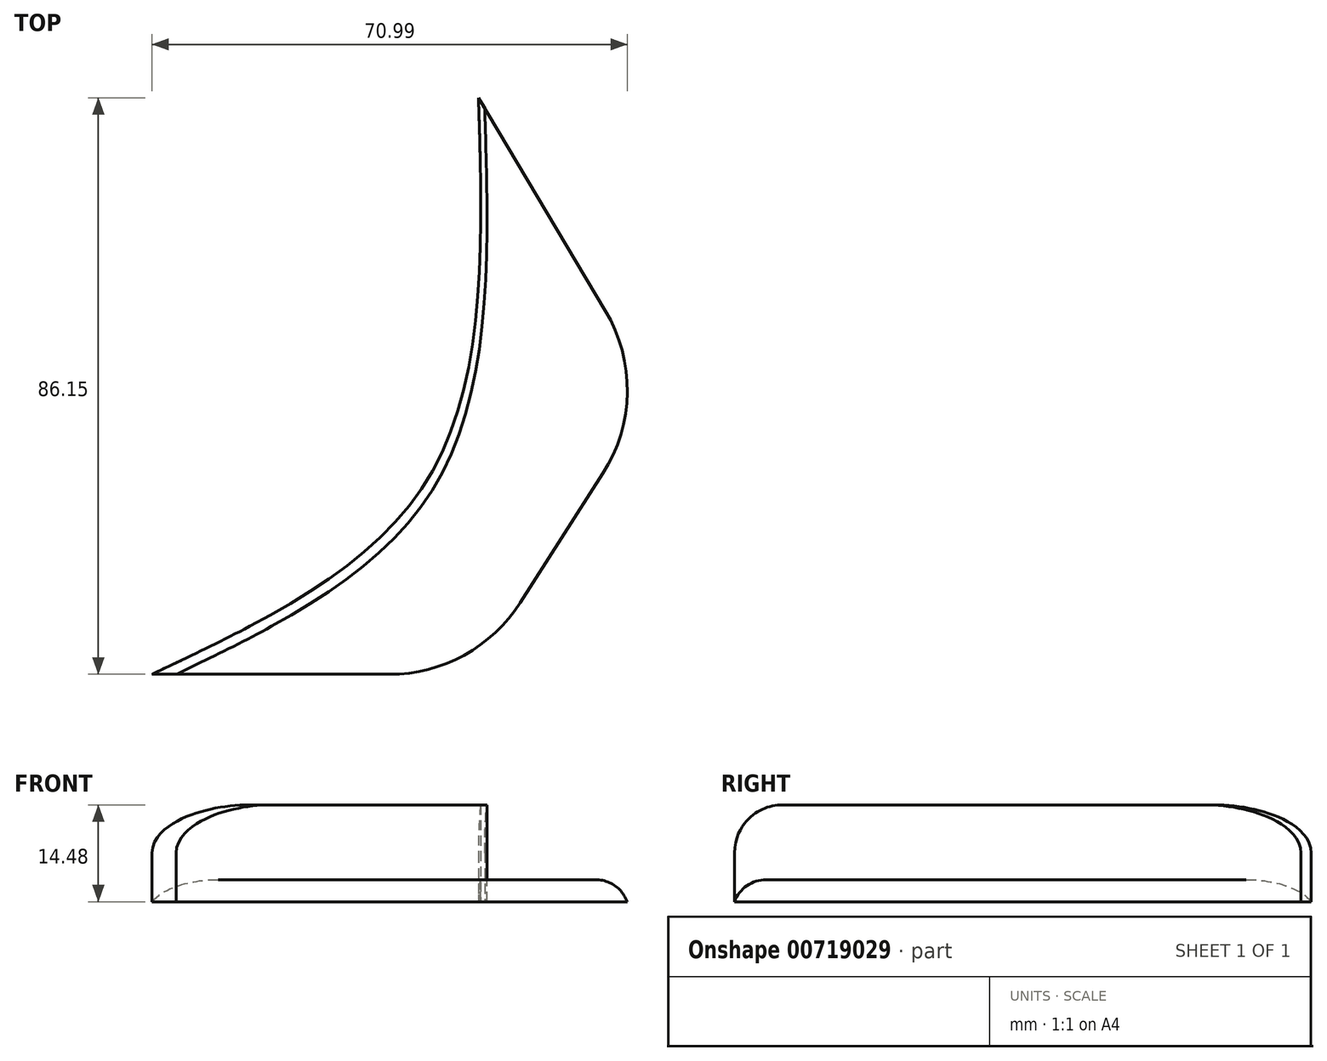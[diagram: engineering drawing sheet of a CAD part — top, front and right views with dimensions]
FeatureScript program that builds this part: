
annotation { "Feature Type Name" : "Feature", "Feature Type Description" : "" }
export const myFeature = defineFeature(function(context is Context, id is Id, definition is map)
    precondition{}
    {
        {
            var Q0;
            Q0=qCreatedBy(makeId("Top.planeOp"),FACE);
            var sketch = newSketch(context, id + "F0", { "sketchPlane" : qUnion([Q0])});
            skFitSpline(sketch, "E0", {"points": [v(-41.32, -29.35) * mm, v(0, 0) * mm, v(7.45, 56.8) * mm], "startDerivative": vector(102.4, 48.5) * mm, "endDerivative": vector(-3.8, 123.02) * mm});
            skLineSegment(sketch, "E1", {"start": v(-41.32, -29.35) * mm, "end": v(6.86, -29.35) * mm});
            skLineSegment(sketch, "E2", {"start": v(6.86, -29.35) * mm, "end": v(33.73, 12.7) * mm});
            skLineSegment(sketch, "E3", {"start": v(33.73, 12.7) * mm, "end": v(7.45, 56.8) * mm});
            skFitSpline(sketch, "E4", {"points": [v(-40.4, -30.62) * mm, v(0.92, -1.27) * mm, v(8.37, 55.53) * mm], "startDerivative": vector(102.4, 48.5) * mm, "endDerivative": vector(-3.8, 123.02) * mm});
            skSolve(sketch);
        }
        {
            var Q0;
            Q0 = qSketchRegion(id + "F0", true);
            extrude(context, id + "F1", {"entities" : qUnion([Q0]), "depth" : 3.3 * mm, "offsetDistance" : 25.4 * mm});
        }
        {
            var Q0;
            {var subQ0=sQuery(id+"F0.wireOp",EDGE,"E0");Q0=makeQuery(id+"F0.imprint","IMPRINT",FACE,{"disambiguationData":[TD([[makeQuery(id+"F0.imprint","IMPRINT",EDGE,{"derivedFrom":subQ0}),-1.0]])]});}
            extrude(context, id + "F2", {"entities" : qUnion([Q0]), "depth" : 14.48 * mm, "offsetDistance" : 25.4 * mm});
        }
        {
            var Q0;
            Q0=makeQuery(id+"F2.opExtrude","CAP_EDGE",EDGE,{"disambiguationData":[OSD([sQuery(id+"F0.wireOp",EDGE,"E1")])],"isStart":false});
            var Q1;
            Q1=makeQuery(id+"F2.opExtrude","CAP_EDGE",EDGE,{"disambiguationData":[OSD([sQuery(id+"F0.wireOp",EDGE,"E3")])],"isStart":false});
            fillet(context, id + "F3", {"entities" : qUnion([Q0, Q1]), "radius" : 7.17 * mm, "tangentPropagation" : true, "allowEdgeOverflow" : false});
        }
        {
            var Q0;
            Q0=makeQuery(id+"F1.opExtrude","SWEPT_EDGE",EDGE,{"disambiguationData":[OSD([sQuery(id+"F0.wireOp",EDGE,"E1"),sQuery(id+"F0.wireOp",EDGE,"E2")])]});
            var Q1;
            Q1=makeQuery(id+"F1.opExtrude","SWEPT_EDGE",EDGE,{"disambiguationData":[OSD([sQuery(id+"F0.wireOp",EDGE,"E2"),sQuery(id+"F0.wireOp",EDGE,"E3")])]});
            fillet(context, id + "F4", {"entities" : qUnion([Q0, Q1]), "radius" : 23.2 * mm, "tangentPropagation" : true, "allowEdgeOverflow" : false});
        }
        {
            var Q0;
            {var subQ0=sQuery(id+"F0.wireOp",EDGE,"E3");var subQ1=sQuery(id+"F0.wireOp",EDGE,"E2");Q0=makeQuery(id+"F4.opFillet","BLEND_EDGE",EDGE,{"blendedFrom":[makeQuery(id+"F1.opExtrude","SWEPT_EDGE",EDGE,{"disambiguationData":[OSD([subQ1,subQ0])]}),makeQuery(id+"F1.opExtrude","CAP_FACE",FACE,{"disambiguationData":[OSD([sQuery(id+"F0.wireOp",EDGE,"E0"),sQuery(id+"F0.wireOp",EDGE,"E1"),subQ1,subQ0])],"isStart":false})],"blendedInto":[makeQuery(id+"F1.opExtrude","CAP_FACE",FACE,{"disambiguationData":[OSD([sQuery(id+"F0.wireOp",EDGE,"E0"),sQuery(id+"F0.wireOp",EDGE,"E1"),subQ1,subQ0])],"isStart":false})]});}
            fillet(context, id + "F5", {"entities" : qUnion([Q0]), "radius" : 5.08 * mm, "tangentPropagation" : true, "allowEdgeOverflow" : false});
        }
    });
